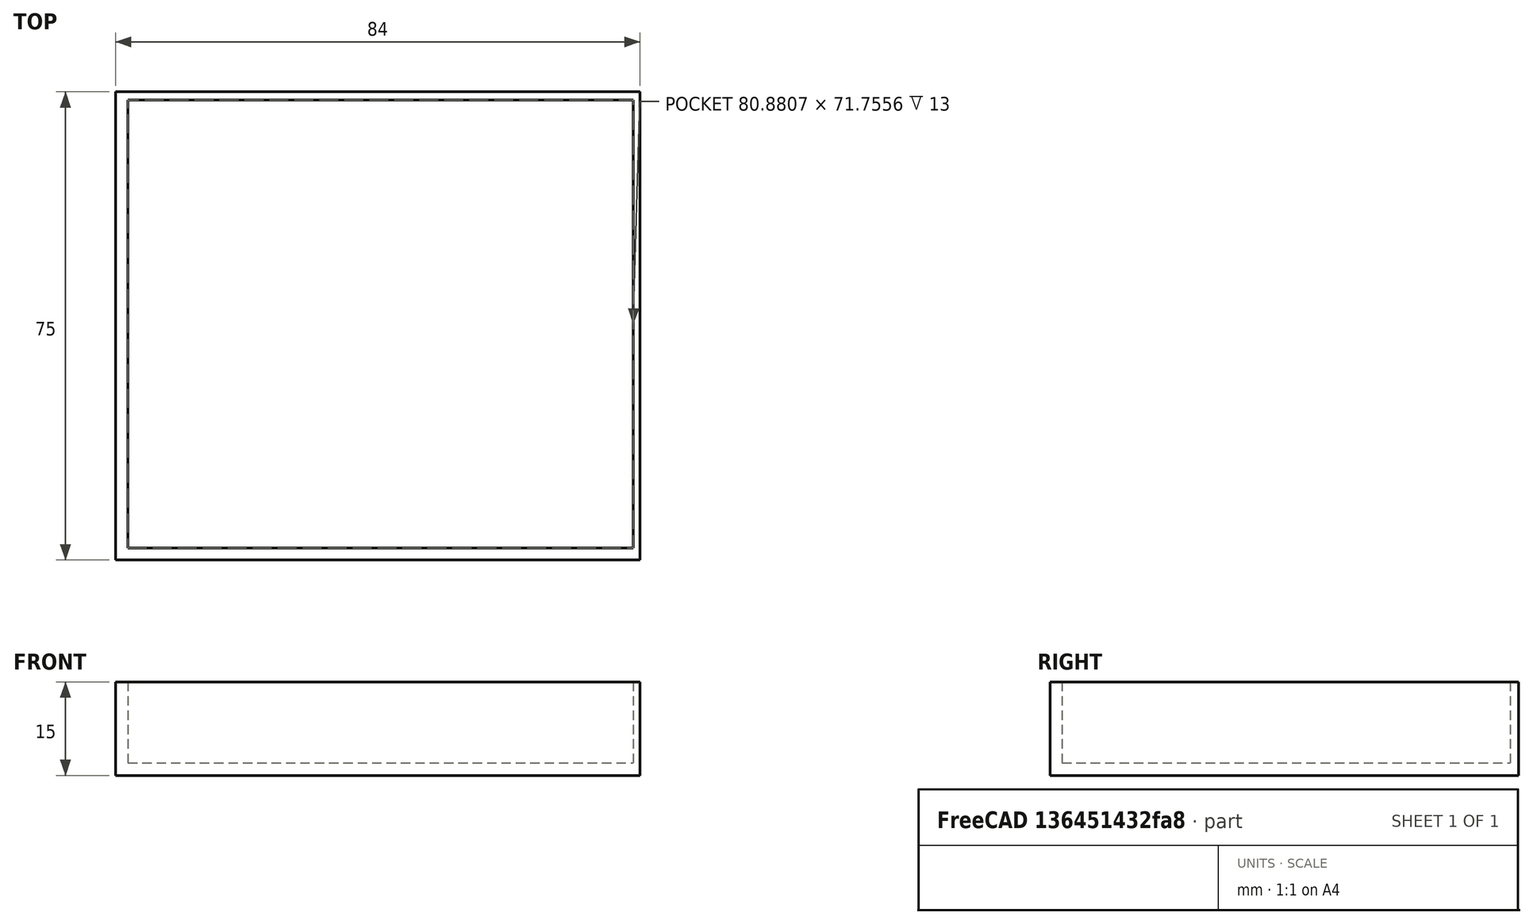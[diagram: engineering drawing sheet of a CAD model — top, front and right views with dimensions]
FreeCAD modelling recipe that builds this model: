
FCSTD DOCUMENT  (FreeCAD 0.19R24267 +148 (Git))
Label: Camera Box
License: All rights reserved
LicenseURL: http://en.wikipedia.org/wiki/All_rights_reserved
objects: Part::Box×1, PartDesign::FeatureBase×1, Sketcher::SketchObject×1, PartDesign::Pocket×1, PartDesign::Body×1
note: 6 computed .brp shape members not serialized (recipe doc carries the construction recipe); baked Part::Feature solids carry a one-line shape summary decoded from their .brp

FEATURE [Part::Box] Box  label="Cube"
  AttacherType = Attacher::AttachEngine3D
  Height = 15
  Length = 84
  Width = 75
FEATURE [PartDesign::FeatureBase] BaseFeature
  BaseFeature = -> Box
FEATURE [Sketcher::SketchObject] Sketch
  FullyConstrained = false
  MapMode = 5
  Placement = pos=(0,0,15) rot=(0,0,1;0rad)
  Support = -> [BaseFeature]
  sketch-geometry (4):
    g0: LineSegment StartX=1.99876 StartY=1.93229 StartZ=0 EndX=82.8795 EndY=1.93229 EndZ=0
    g1: LineSegment StartX=82.8795 StartY=1.93229 StartZ=0 EndX=82.8795 EndY=73.6879 EndZ=0
    g2: LineSegment StartX=82.8795 StartY=73.6879 StartZ=0 EndX=1.99876 EndY=73.6879 EndZ=0
    g3: LineSegment StartX=1.99876 StartY=73.6879 StartZ=0 EndX=1.99876 EndY=1.93229 EndZ=0
  constraints (8):
    c: Coincident(g0,g1)
    c: Coincident(g1,g2)
    c: Coincident(g2,g3)
    c: Coincident(g3,g0)
    c: Horizontal(g0)
    c: Horizontal(g2)
    c: Vertical(g1)
    c: Vertical(g3)
FEATURE [PartDesign::Pocket] Pocket
  BaseFeature = -> BaseFeature
  Length = 13
  Length2 = 100
  Profile = -> Sketch
  Type = 0
FEATURE [PartDesign::Body] Body
  BaseFeature = -> Box
  Group = -> [BaseFeature,Sketch,Pocket]
  Origin = -> Origin
  Tip = -> Pocket
